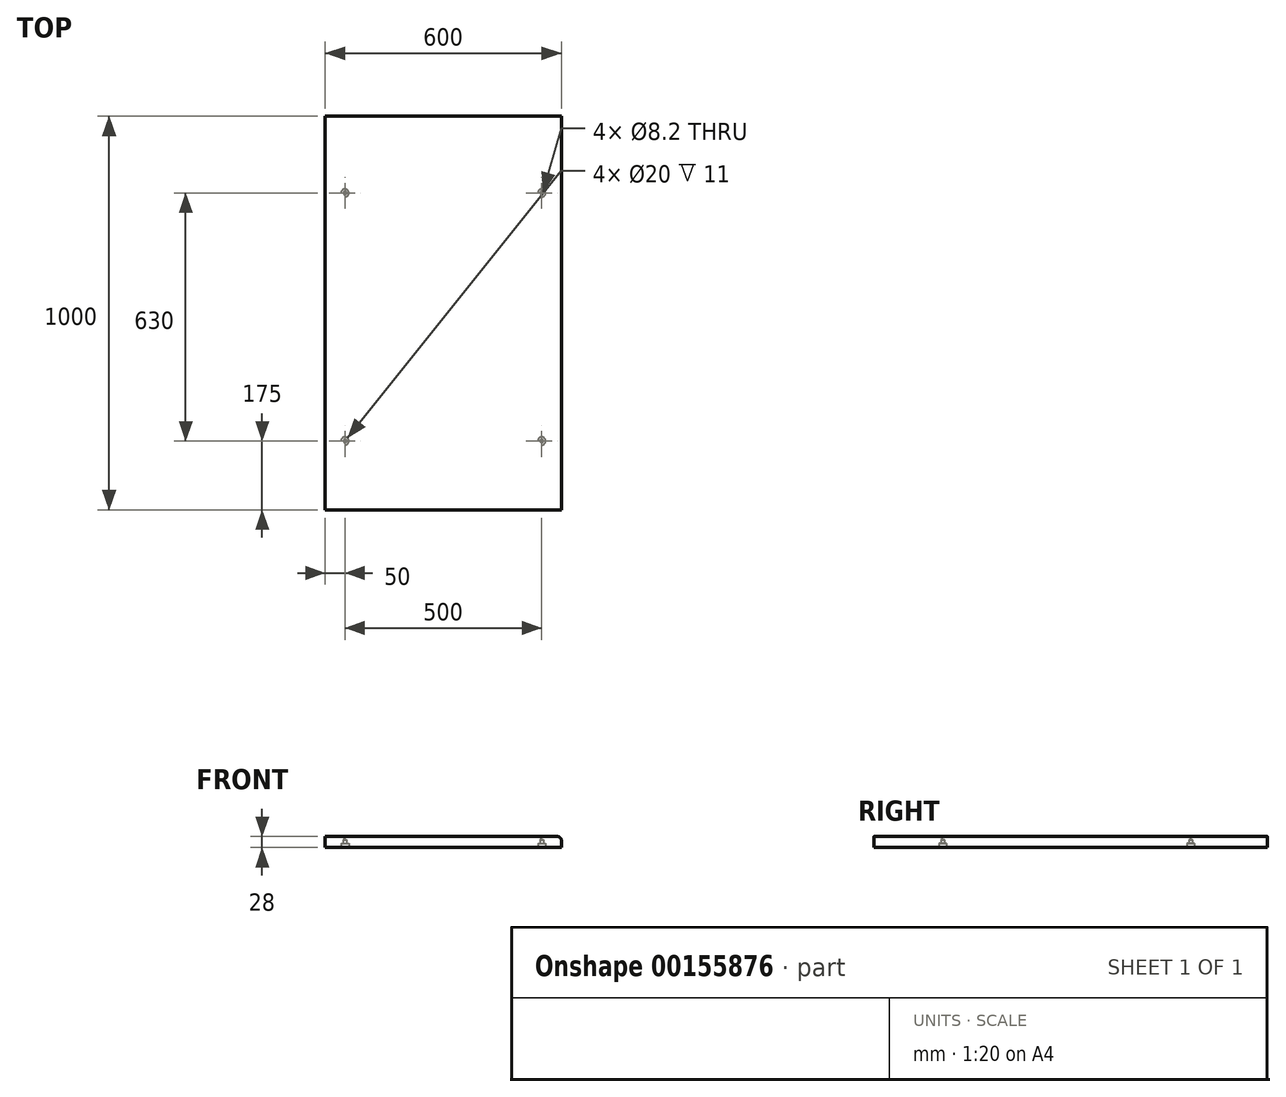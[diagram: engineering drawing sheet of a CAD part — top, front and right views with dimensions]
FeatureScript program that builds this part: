
annotation { "Feature Type Name" : "Feature", "Feature Type Description" : "" }
export const myFeature = defineFeature(function(context is Context, id is Id, definition is map)
    precondition{}
    {
        {
            var Q0;
            Q0=qCreatedBy(makeId("Top.planeOp"),FACE);
            cPlane(context, id + "F0", {"entities" : qUnion([Q0]), "cplaneType" : CPlaneType.OFFSET, "offset" : 850 * mm, "width" : 150 * mm, "height" : 150 * mm});
        }
        {
            var Q0;
            Q0=qCreatedBy(id+"F0.planeOp",FACE);
            var sketch = newSketch(context, id + "F1", { "sketchPlane" : qUnion([Q0])});
            skLineSegment(sketch, "E0.bottom", {"start": v(-300, 500) * mm, "end": v(300, 500) * mm});
            skLineSegment(sketch, "E0.top", {"start": v(-300, -500) * mm, "end": v(300, -500) * mm});
            skLineSegment(sketch, "E0.left", {"start": v(-300, 500) * mm, "end": v(-300, -500) * mm});
            skLineSegment(sketch, "E0.right", {"start": v(300, 500) * mm, "end": v(300, -500) * mm});
            skPoint(sketch, "E0.middle", {"position": v(0, 0) * mm});
            skSolve(sketch);
        }
        {
            var Q0;
            Q0=makeQuery(id+"F1.imprint","IMPRINT",FACE,{"disambiguationData":[TD([[makeQuery(id+"F1.imprint","IMPRINT",EDGE,{"derivedFrom":sQuery(id+"F1.wireOp",EDGE,"E0.bottom")}),-1.0]])]});
            extrude(context, id + "F2", {"entities" : qUnion([Q0]), "depth" : 28 * mm});
        }
        {
            var Q0;
            Q0=makeQuery(id+"F2.opExtrude","CAP_EDGE",EDGE,{"disambiguationData":[OSD([sQuery(id+"F1.wireOp",EDGE,"E0.right")])],"isStart":false});
            fillet(context, id + "F3", {"entities" : qUnion([Q0]), "radius" : 10 * mm, "tangentPropagation" : true, "allowEdgeOverflow" : false});
        }
        {
            var Q0;
            Q0=qCreatedBy(id+"F0.planeOp",FACE);
            var sketch = newSketch(context, id + "F4", { "sketchPlane" : qUnion([Q0])});
            skPoint(sketch, "E1", {"position": v(250, -325) * mm});
            skPoint(sketch, "E2", {"position": v(250, 305) * mm});
            skPoint(sketch, "E3", {"position": v(-250, -325) * mm});
            skPoint(sketch, "E4", {"position": v(-250, 305) * mm});
            skSolve(sketch);
        }
        {
            var Q0;
            Q0=sQuery(id+"F4.wireOp",VERTEX,"E1");
            var Q1;
            Q1=sQuery(id+"F4.wireOp",VERTEX,"E2");
            var Q2;
            Q2=sQuery(id+"F4.wireOp",VERTEX,"E4");
            var Q3;
            Q3=sQuery(id+"F4.wireOp",VERTEX,"E3");
            var Q4;
            Q4=makeQuery(id+"F2.opExtrude","SWEPT_BODY",BODY,{"disambiguationData":[OSD([sQuery(id+"F1.wireOp",EDGE,"E0.bottom"),sQuery(id+"F1.wireOp",EDGE,"E0.top"),sQuery(id+"F1.wireOp",EDGE,"E0.left"),sQuery(id+"F1.wireOp",EDGE,"E0.right")])]});
            hole(context, id + "F5", {"style" : HoleStyle.C_BORE, "endStyle" : HoleEndStyle.BLIND, "oppositeDirection" : true, "holeDiameter" : 8.2 * mm, "cBoreDiameter" : 20 * mm, "cBoreDepth" : 11 * mm, "holeDepth" : 20 * mm, "locations" : qUnion([Q0, Q1, Q2, Q3]), "scope" : qUnion([Q4])});
        }
    });
